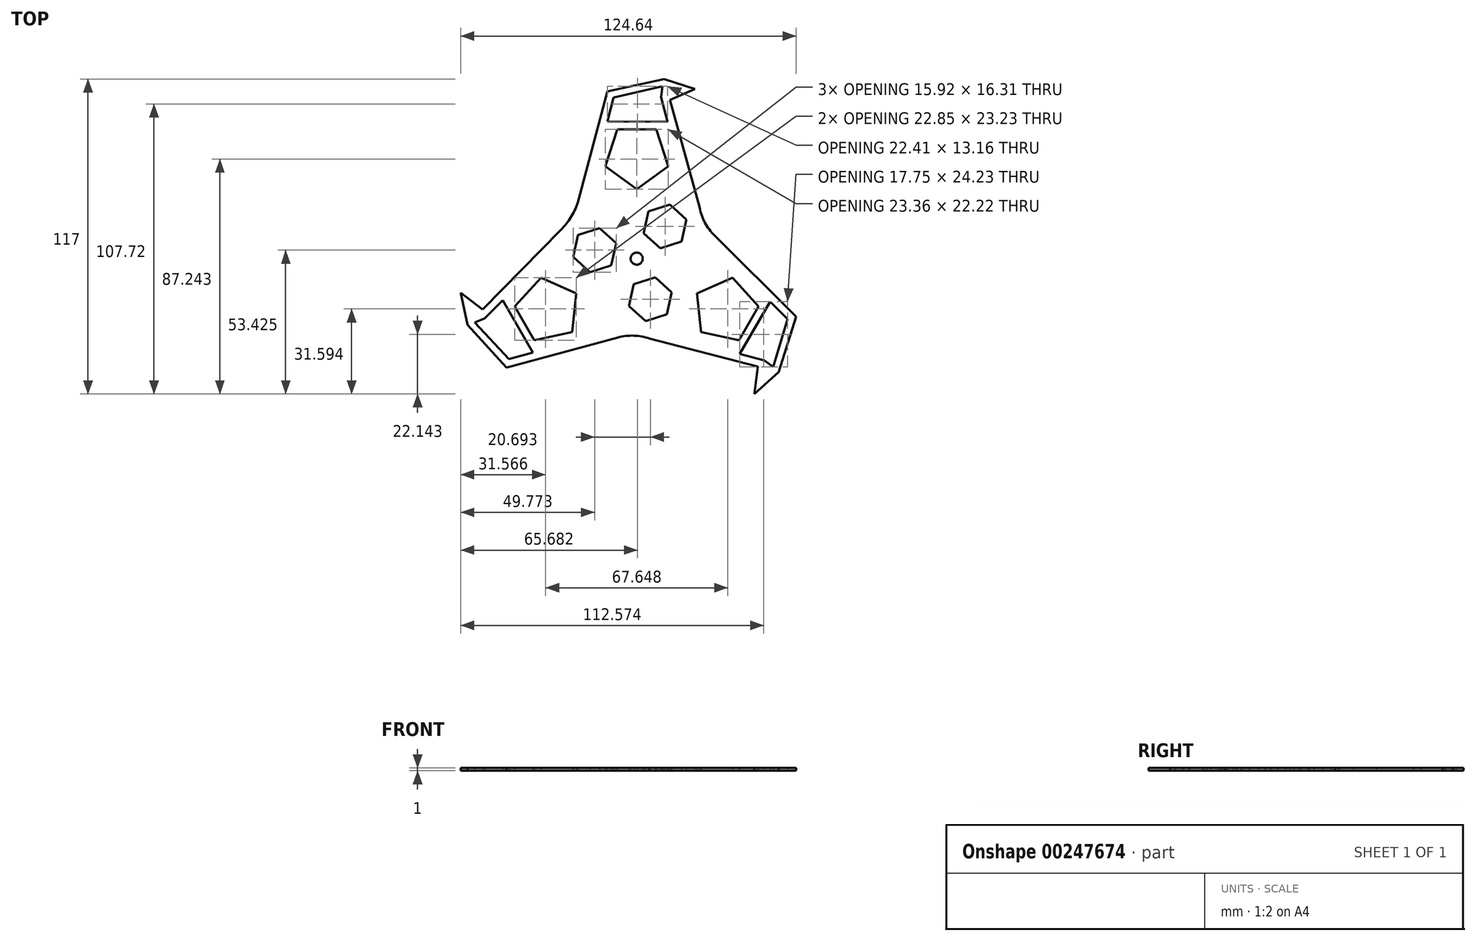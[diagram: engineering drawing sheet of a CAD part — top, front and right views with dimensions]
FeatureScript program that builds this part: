
annotation { "Feature Type Name" : "Feature", "Feature Type Description" : "" }
export const myFeature = defineFeature(function(context is Context, id is Id, definition is map)
    precondition{}
    {
        {
            var Q0;
            Q0=qCreatedBy(makeId("Top.planeOp"),FACE);
            var sketch = newSketch(context, id + "F0", { "sketchPlane" : qUnion([Q0])});
            skCircle(sketch, "E0", {"center": v(0, 0) * mm, "radius": 2.25 * mm});
            skLineSegment(sketch, "E1", {"start": v(10.14, 66.73) * mm, "end": v(-10.94, 62.1) * mm});
            skLineSegment(sketch, "E2", {"start": v(-10.94, 62.1) * mm, "end": v(-21.9, 20.66) * mm});
            skLineSegment(sketch, "E3", {"start": v(10.14, 66.73) * mm, "end": v(21.68, 63) * mm});
            skLineSegment(sketch, "E4", {"start": v(21.68, 63) * mm, "end": v(12.3, 59.01) * mm});
            skLineSegment(sketch, "E5", {"start": v(12.3, 59.01) * mm, "end": v(23.36, 19) * mm});
            skLineSegment(sketch, "E6.1.0", {"start": v(-48.3, -40.52) * mm, "end": v(-6.94, -29.3) * mm});
            skLineSegment(sketch, "E6.1.1", {"start": v(-62.86, -24.59) * mm, "end": v(-48.3, -40.52) * mm});
            skLineSegment(sketch, "E6.1.2", {"start": v(-62.86, -24.59) * mm, "end": v(-65.4, -12.72) * mm});
            skLineSegment(sketch, "E6.1.3", {"start": v(-65.4, -12.72) * mm, "end": v(-57.26, -18.85) * mm});
            skLineSegment(sketch, "E6.1.4", {"start": v(-57.26, -18.85) * mm, "end": v(-28.13, 10.72) * mm});
            skLineSegment(sketch, "E6.2.0", {"start": v(59.25, -21.57) * mm, "end": v(28.84, 8.64) * mm});
            skLineSegment(sketch, "E6.2.1", {"start": v(52.72, -42.15) * mm, "end": v(59.25, -21.57) * mm});
            skLineSegment(sketch, "E6.2.2", {"start": v(52.72, -42.15) * mm, "end": v(43.71, -50.27) * mm});
            skLineSegment(sketch, "E6.2.3", {"start": v(43.71, -50.27) * mm, "end": v(44.95, -40.16) * mm});
            skLineSegment(sketch, "E6.2.4", {"start": v(44.95, -40.16) * mm, "end": v(4.78, -29.73) * mm});
            skArc(sketch, "E7", {"start": v(-28.13, 10.72) * mm, "mid": v(-24.48, 15.35) * mm, "end": v(-21.9, 20.66) * mm});
            skArc(sketch, "E8", {"start": v(4.78, -29.73) * mm, "mid": v(-1.05, -28.62) * mm, "end": v(-6.94, -29.3) * mm});
            skArc(sketch, "E9", {"start": v(23.36, 19) * mm, "mid": v(25.31, 13.4) * mm, "end": v(28.84, 8.64) * mm});
            skPoint(sketch, "E10.0.midPoint", {"position": v(-4.98, 3.15) * mm});
            skLineSegment(sketch, "E11.0", {"start": v(-7.22, 48.08) * mm, "end": v(7.22, 48.08) * mm});
            skLineSegment(sketch, "E11.1", {"start": v(7.22, 48.08) * mm, "end": v(11.68, 34.35) * mm});
            skLineSegment(sketch, "E11.2", {"start": v(11.68, 34.35) * mm, "end": v(0, 25.86) * mm});
            skLineSegment(sketch, "E11.3", {"start": v(0, 25.86) * mm, "end": v(-11.68, 34.35) * mm});
            skLineSegment(sketch, "E11.4", {"start": v(-11.68, 34.35) * mm, "end": v(-7.22, 48.08) * mm});
            skPoint(sketch, "E11.0.midPoint", {"position": v(0, 48.08) * mm});
            skLineSegment(sketch, "E12.1.0", {"start": v(-23.9, -27.3) * mm, "end": v(-38.03, -30.3) * mm});
            skLineSegment(sketch, "E12.1.1", {"start": v(-38.03, -30.3) * mm, "end": v(-45.25, -17.79) * mm});
            skLineSegment(sketch, "E12.1.2", {"start": v(-45.25, -17.79) * mm, "end": v(-35.59, -7.06) * mm});
            skLineSegment(sketch, "E12.1.3", {"start": v(-35.59, -7.06) * mm, "end": v(-22.4, -12.93) * mm});
            skLineSegment(sketch, "E12.1.4", {"start": v(-22.4, -12.93) * mm, "end": v(-23.9, -27.3) * mm});
            skLineSegment(sketch, "E12.2.0", {"start": v(35.59, -7.06) * mm, "end": v(45.25, -17.79) * mm});
            skLineSegment(sketch, "E12.2.1", {"start": v(45.25, -17.79) * mm, "end": v(38.03, -30.3) * mm});
            skLineSegment(sketch, "E12.2.2", {"start": v(38.03, -30.3) * mm, "end": v(23.9, -27.3) * mm});
            skLineSegment(sketch, "E12.2.3", {"start": v(23.9, -27.3) * mm, "end": v(22.4, -12.93) * mm});
            skLineSegment(sketch, "E12.2.4", {"start": v(22.4, -12.93) * mm, "end": v(35.59, -7.06) * mm});
            skLineSegment(sketch, "E13", {"start": v(-60.2, -23.79) * mm, "end": v(-47.5, -37.31) * mm});
            skLineSegment(sketch, "E14", {"start": v(-47.5, -37.31) * mm, "end": v(-38.64, -34.91) * mm});
            skPoint(sketch, "E14.endSnap0", {"position": v(-27.62, -34.91) * mm});
            skLineSegment(sketch, "E15", {"start": v(-38.64, -34.91) * mm, "end": v(-49.8, -15.48) * mm});
            skLineSegment(sketch, "E16", {"start": v(-49.8, -15.48) * mm, "end": v(-56.48, -22.16) * mm});
            skLineSegment(sketch, "E17.1.0", {"start": v(38.3, -35.4) * mm, "end": v(47.43, -37.84) * mm});
            skLineSegment(sketch, "E17.1.1", {"start": v(49.55, -16) * mm, "end": v(38.3, -35.4) * mm});
            skLineSegment(sketch, "E17.1.2", {"start": v(56.06, -22.47) * mm, "end": v(49.55, -16) * mm});
            skLineSegment(sketch, "E17.1.3", {"start": v(50.7, -40.24) * mm, "end": v(56.06, -22.47) * mm});
            skLineSegment(sketch, "E17.2.0", {"start": v(11.5, 50.87) * mm, "end": v(9.05, 60) * mm});
            skLineSegment(sketch, "E17.2.1", {"start": v(-10.91, 50.92) * mm, "end": v(11.5, 50.87) * mm});
            skLineSegment(sketch, "E17.2.2", {"start": v(-8.57, 59.79) * mm, "end": v(-10.91, 50.92) * mm});
            skLineSegment(sketch, "E17.2.3", {"start": v(9.5, 64.03) * mm, "end": v(-8.57, 59.79) * mm});
            skLineSegment(sketch, "E18", {"start": v(9.5, 64.03) * mm, "end": v(9.05, 60) * mm});
            skLineSegment(sketch, "E19", {"start": v(-60.2, -23.79) * mm, "end": v(-56.48, -22.16) * mm});
            skLineSegment(sketch, "E20", {"start": v(47.43, -37.84) * mm, "end": v(50.7, -40.24) * mm});
            skCircle(sketch, "E21.cCircle", {"center": v(-15.62, 3.15) * mm, "radius": 7.23 * mm, "construction": true});
            skLineSegment(sketch, "E21.0", {"start": v(-13.82, 11.31) * mm, "end": v(-7.66, 5.67) * mm});
            skLineSegment(sketch, "E21.1", {"start": v(-7.66, 5.67) * mm, "end": v(-9.45, -2.48) * mm});
            skLineSegment(sketch, "E21.2", {"start": v(-9.45, -2.48) * mm, "end": v(-17.42, -5) * mm});
            skLineSegment(sketch, "E21.3", {"start": v(-17.42, -5) * mm, "end": v(-23.58, 0.64) * mm});
            skLineSegment(sketch, "E21.4", {"start": v(-23.58, 0.64) * mm, "end": v(-21.78, 8.8) * mm});
            skLineSegment(sketch, "E21.5", {"start": v(-21.78, 8.8) * mm, "end": v(-13.82, 11.31) * mm});
            skPoint(sketch, "E21.0.midPoint", {"position": v(-10.74, 8.5) * mm});
            skLineSegment(sketch, "E22.1.0", {"start": v(-2.89, -17.62) * mm, "end": v(-1.09, -9.47) * mm});
            skLineSegment(sketch, "E22.1.1", {"start": v(3.28, -23.26) * mm, "end": v(-2.89, -17.62) * mm});
            skLineSegment(sketch, "E22.1.2", {"start": v(11.24, -20.74) * mm, "end": v(3.28, -23.26) * mm});
            skLineSegment(sketch, "E22.1.3", {"start": v(13.04, -12.58) * mm, "end": v(11.24, -20.74) * mm});
            skLineSegment(sketch, "E22.1.4", {"start": v(6.88, -6.95) * mm, "end": v(13.04, -12.58) * mm});
            skLineSegment(sketch, "E22.1.5", {"start": v(-1.09, -9.47) * mm, "end": v(6.88, -6.95) * mm});
            skLineSegment(sketch, "E22.2.0", {"start": v(16.7, 6.31) * mm, "end": v(8.74, 3.8) * mm});
            skLineSegment(sketch, "E22.2.1", {"start": v(18.5, 14.47) * mm, "end": v(16.7, 6.31) * mm});
            skLineSegment(sketch, "E22.2.2", {"start": v(12.34, 20.1) * mm, "end": v(18.5, 14.47) * mm});
            skLineSegment(sketch, "E22.2.3", {"start": v(4.38, 17.58) * mm, "end": v(12.34, 20.1) * mm});
            skLineSegment(sketch, "E22.2.4", {"start": v(2.58, 9.43) * mm, "end": v(4.38, 17.58) * mm});
            skLineSegment(sketch, "E22.2.5", {"start": v(8.74, 3.8) * mm, "end": v(2.58, 9.43) * mm});
            skSolve(sketch);
        }
        {
            var Q0;
            Q0=makeQuery(id+"F0.imprint","IMPRINT",FACE,{"disambiguationData":[TD([[makeQuery(id+"F0.imprint","IMPRINT",EDGE,{"derivedFrom":sQuery(id+"F0.wireOp",EDGE,"E0")}),-1.0]])]});
            extrude(context, id + "F1", {"entities" : qUnion([Q0]), "depth" : 1 * mm});
        }
    });
